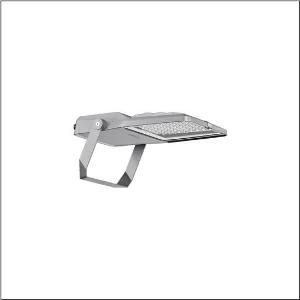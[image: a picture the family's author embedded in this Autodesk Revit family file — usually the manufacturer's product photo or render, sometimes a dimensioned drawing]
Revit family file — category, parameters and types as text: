
# Revit family: floodlight_fl_21_mini___pl61_5xa7775b2c1a_33c0
name_source: partatom
category: Lighting Fixtures
units: mm (PartAtom-declared; Revit-internal decimal feet)

## family parameters
Cut with Voids When Loaded = No
Host = Face
Light Source = No
Part Type = Normal
Room Calculation Point = No
Round Connector Dimension = Use Diameter
Shared = No

## types (1)
- --- (1 x LED, 6110 lm, 45.7 W, 3000K)
    Apparent Load = 46 VA
    CIE Flux Codes = 33 65 98 100 100
    Color Rendering = 70
    Color Temperature = 3000K
    Default Elevation = 1800 mm
    Description = Floodlight FL 21 mini, floodlight, primary light control with lens, of PMMA, primary optical cover: protective disc, of toughened safety glass, transparent, light distribution: PL61, light emission: direct distribution, installation type: surface-mounted, LED, High Power LED, rated luminous flux: 6.110lm, luminous efficacy: 134lm/W, light colour: 730, colour temperature: 3000K, control: flexible luminous flux parameterisation, time-dependent luminous flux control, constant luminous flux control, overheat protection, presetting dimming logarithmic, with terminal, 6-pole, mains connection: 220..240V, AC, 50/60Hz, start of lifetime: 46W, end of service life: 48W, reduction: 22W, luminaire housing, of diecast aluminium, powder-coated, Siteco® metallic grey (DB 702S), corrosivity category C5 mid according to DIN EN ISO 12944, sealing non-destructively replaceable, mounting bracket, of steel, galvanised, powder-coated, Siteco® metallic grey (DB 702S), Smart Interface above, protection rating (complete): IP66, insulation class (complete): insulation class II (safety insulation), certification: CE, ENEC, VDE, protection symbol: D, impact resistance: IK08, permissible operating ambient temperature: -40..+40°C, permissible operating ambient temperature for outdoor applications: -40..+50°C, standard: DIN EN 12944, LABS conformity tested according to VDMA 24364:2018-05, packaging unit: 1 piece

Light Distribution: PL61
    Height = 70 mm
    Lamp = 1 x LED
    Lamp Light Flux = 6110 lm
    Lamp Power = 45.7 W
    Lamp count = 1
    Length = 485 mm
    Luminous efficacy = 134 lm/W
    Manufacturer = Siteco
    ModVariant = No
    Model = 5XA7775B2C1A
    Number of Poles = 1
    OnlyDefault = Yes
    Power Factor = 1
    Product Name = Floodlight FL 21 mini | PL61
    Product group = floodlight | pylon annexe
    ProductGroupID = 6200
    Protection Class = Protection class II
    Protection Degree = IP 66
    RLX_Detail_Level = 1
    RLX_Emergency_Light_Flux = 0 lm
    RLX_Emergency_Type = 0
    RLX_Emergency_Type_DB = No
    RlxData = <blob elided: 95833 chars, md5=671301e7>
    Socket = socket
    Standby Power = 0 W
    System Light Flux = 6110 lm
    System Power = 46 W
    Type Comments = factory setting: luminous flux: 100 % | dim-lin: 254 | 463 mA
    Type Image = l_1006845.jpg
    URL = http://relux.com
    VarID = @adj_123155
    Voltage = 0 V
    Weight = 0.00 kg
    Width = 337 mm

## geometry (parser evidence)
native form markers: Blend x4, Sweep x12
no freeform markers — native parametric forms only
